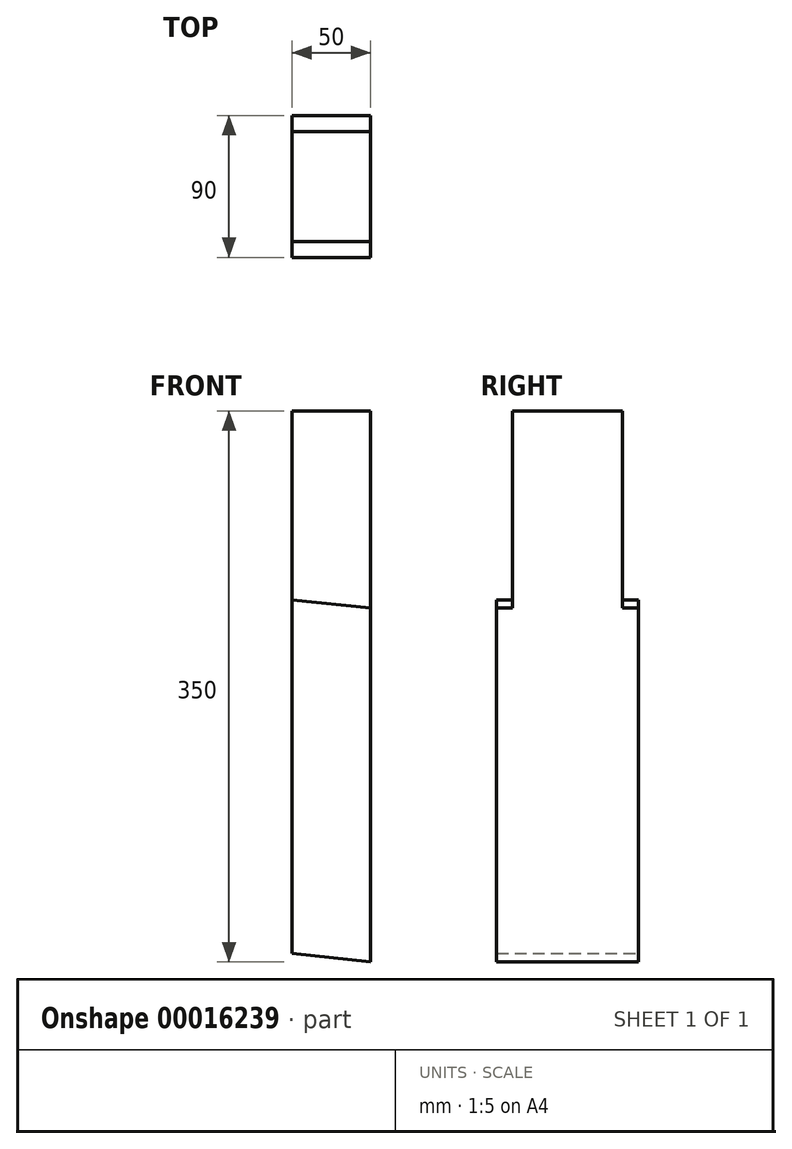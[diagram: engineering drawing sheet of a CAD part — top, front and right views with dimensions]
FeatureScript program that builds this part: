
annotation { "Feature Type Name" : "Feature", "Feature Type Description" : "" }
export const myFeature = defineFeature(function(context is Context, id is Id, definition is map)
    precondition{}
    {
        {
            var Q0;
            Q0=qCreatedBy(makeId("Right.planeOp"),FACE);
            var sketch = newSketch(context, id + "F0", { "sketchPlane" : qUnion([Q0])});
            skLineSegment(sketch, "E0.bottom", {"start": v(-122.41, 167.48) * mm, "end": v(-32.41, 167.48) * mm});
            skLineSegment(sketch, "E0.top", {"start": v(-122.41, -182.52) * mm, "end": v(-32.41, -182.52) * mm});
            skLineSegment(sketch, "E0.left", {"start": v(-122.41, 167.48) * mm, "end": v(-122.41, -182.52) * mm});
            skLineSegment(sketch, "E0.right", {"start": v(-32.41, 167.48) * mm, "end": v(-32.41, -182.52) * mm});
            skSolve(sketch);
        }
        {
            var Q0;
            Q0=makeQuery(id+"F0.imprint","IMPRINT",FACE,{"disambiguationData":[TD([[makeQuery(id+"F0.imprint","IMPRINT",EDGE,{"derivedFrom":sQuery(id+"F0.wireOp",EDGE,"E0.bottom")}),-1.0]])]});
            extrude(context, id + "F1", {"entities" : qUnion([Q0]), "depth" : 50 * mm});
        }
        {
            var Q0;
            Q0=makeQuery(id+"F1.opExtrude","SWEPT_FACE",FACE,{"disambiguationData":[OSD([sQuery(id+"F0.wireOp",EDGE,"E0.left")])]});
            var sketch = newSketch(context, id + "F2", { "sketchPlane" : qUnion([Q0])});
            skLineSegment(sketch, "E1", {"start": v(0, 167.48) * mm, "end": v(50, 167.48) * mm});
            skLineSegment(sketch, "E2", {"start": v(50, 167.48) * mm, "end": v(50, 42.22) * mm});
            skLineSegment(sketch, "E3", {"start": v(50, 42.22) * mm, "end": v(0, 47.48) * mm});
            skLineSegment(sketch, "E4", {"start": v(0, 47.48) * mm, "end": v(0, 167.48) * mm});
            skSolve(sketch);
        }
        {
            var Q0;
            {var subQ6=sQuery(id+"F2.wireOp",EDGE,"E4");Q0=makeQuery(id+"F2.imprint","IMPRINT",FACE,{"disambiguationData":[TD([[makeQuery(id+"F2.imprint","IMPRINT",EDGE,{"derivedFrom":subQ6}),1.0]])]});}
            extrude(context, id + "F3", {"entities" : qUnion([Q0]), "operationType" : NewBodyOperationType.REMOVE, "oppositeDirection" : true, "depth" : 10 * mm});
        }
        {
            var Q0;
            Q0=makeQuery(id+"F1.opExtrude","SWEPT_FACE",FACE,{"disambiguationData":[OSD([sQuery(id+"F0.wireOp",EDGE,"E0.right")])]});
            var sketch = newSketch(context, id + "F4", { "sketchPlane" : qUnion([Q0])});
            skLineSegment(sketch, "E5", {"start": v(0, 167.48) * mm, "end": v(-50, 167.48) * mm});
            skLineSegment(sketch, "E6", {"start": v(-50, 167.48) * mm, "end": v(-50, 42.22) * mm});
            skLineSegment(sketch, "E7", {"start": v(-50, 42.22) * mm, "end": v(0, 47.48) * mm});
            skLineSegment(sketch, "E8", {"start": v(0, 47.48) * mm, "end": v(0, 167.48) * mm});
            skSolve(sketch);
        }
        {
            var Q0;
            {var subQ6=sQuery(id+"F4.wireOp",EDGE,"E8");Q0=makeQuery(id+"F4.imprint","IMPRINT",FACE,{"disambiguationData":[TD([[makeQuery(id+"F4.imprint","IMPRINT",EDGE,{"derivedFrom":subQ6}),-1.0]])]});}
            extrude(context, id + "F5", {"entities" : qUnion([Q0]), "operationType" : NewBodyOperationType.REMOVE, "oppositeDirection" : true, "depth" : 10 * mm});
        }
        {
            var Q0;
            Q0=makeQuery(id+"F1.opExtrude","SWEPT_FACE",FACE,{"disambiguationData":[OSD([sQuery(id+"F0.wireOp",EDGE,"E0.right")])]});
            var sketch = newSketch(context, id + "F6", { "sketchPlane" : qUnion([Q0])});
            skLineSegment(sketch, "E9", {"start": v(-50, -182.52) * mm, "end": v(0, -177.27) * mm});
            skLineSegment(sketch, "E10", {"start": v(0, -177.27) * mm, "end": v(0, -182.52) * mm});
            skLineSegment(sketch, "E11", {"start": v(0, -182.52) * mm, "end": v(-50, -182.52) * mm});
            skSolve(sketch);
        }
        {
            var Q0;
            Q0=makeQuery(id+"F6.imprint","IMPRINT",FACE,{"disambiguationData":[TD([[makeQuery(id+"F6.imprint","IMPRINT",EDGE,{"derivedFrom":sQuery(id+"F6.wireOp",EDGE,"E9")}),-1.0]])]});
            extrude(context, id + "F7", {"entities" : qUnion([Q0]), "operationType" : NewBodyOperationType.REMOVE, "endBound" : BoundingType.THROUGH_ALL, "oppositeDirection" : true, "depth" : 25 * mm});
        }
    });
